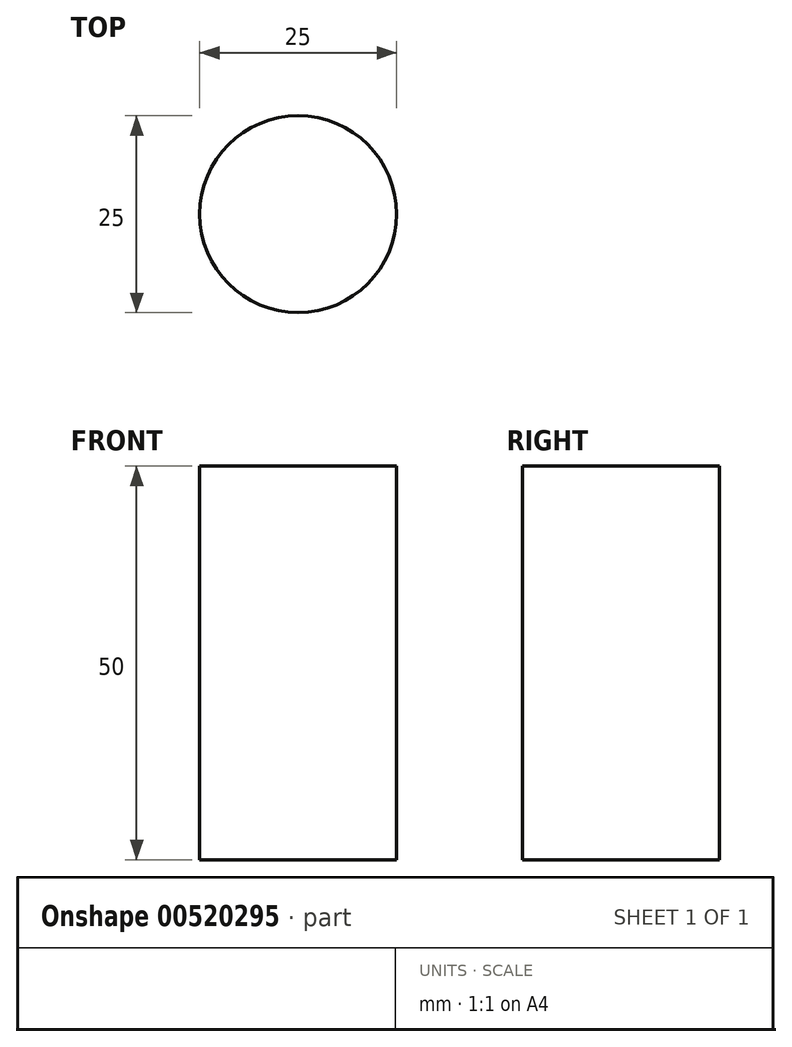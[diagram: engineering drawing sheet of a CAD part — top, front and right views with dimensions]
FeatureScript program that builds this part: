
annotation { "Feature Type Name" : "Feature", "Feature Type Description" : "" }
export const myFeature = defineFeature(function(context is Context, id is Id, definition is map)
    precondition{}
    {
        {
            var Q0;
            Q0=qCreatedBy(makeId("Top.planeOp"),FACE);
            var sketch = newSketch(context, id + "F0", { "sketchPlane" : qUnion([Q0])});
            skCircle(sketch, "E0", {"center": v(0, 0) * mm, "radius": 12.5 * mm});
            skSolve(sketch);
        }
        {
            var Q0;
            Q0=sQuery(id+"F0.wireOp",EDGE,"E0");
            extrude(context, id + "F1", {"bodyType" : ToolBodyType.SURFACE, "surfaceEntities" : qUnion([Q0]), "depth" : 50 * mm, "offsetDistance" : 25.4 * mm});
        }
    });
